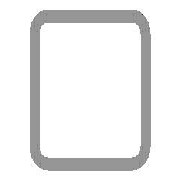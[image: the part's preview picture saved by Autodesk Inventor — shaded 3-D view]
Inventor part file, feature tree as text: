
AUTODESK INVENTOR PART (.ipt)
format: ipt  version: 2025 (Build 290162010, 162A)  size: 134,656 bytes
history: native  units: mm (DEFAULTED — no unit token found)
features: other x4, sketch x1, plane x1
ambient origin geometry x8: Origin, YZ Plane, XZ Plane, XY Plane, X Axis, Y Axis, Z Axis, Center Point
bodies: Solid1 (feature_tree), Body (feature_tree)
feature tree (6):
  parser-record x1  (decoder bookkeeping rows leaked as tree rows — omitted from the tree; the rows remain in map.json)
  other  "Driven Length"
  other  "Start Plane"
  other  "End Plane"
  sketch  "Sketch3"  dims[d3=1105.0mm d4=0.0mm d7=6.0mm d9=80.0mm d11=80.0mm d12=3.0mm d13=-0.0mm d14=1105.0mm d15=40.0mm d16=40.0mm d17=90.0deg d18=1105.0mm]
  plane  "Work Plane3"
